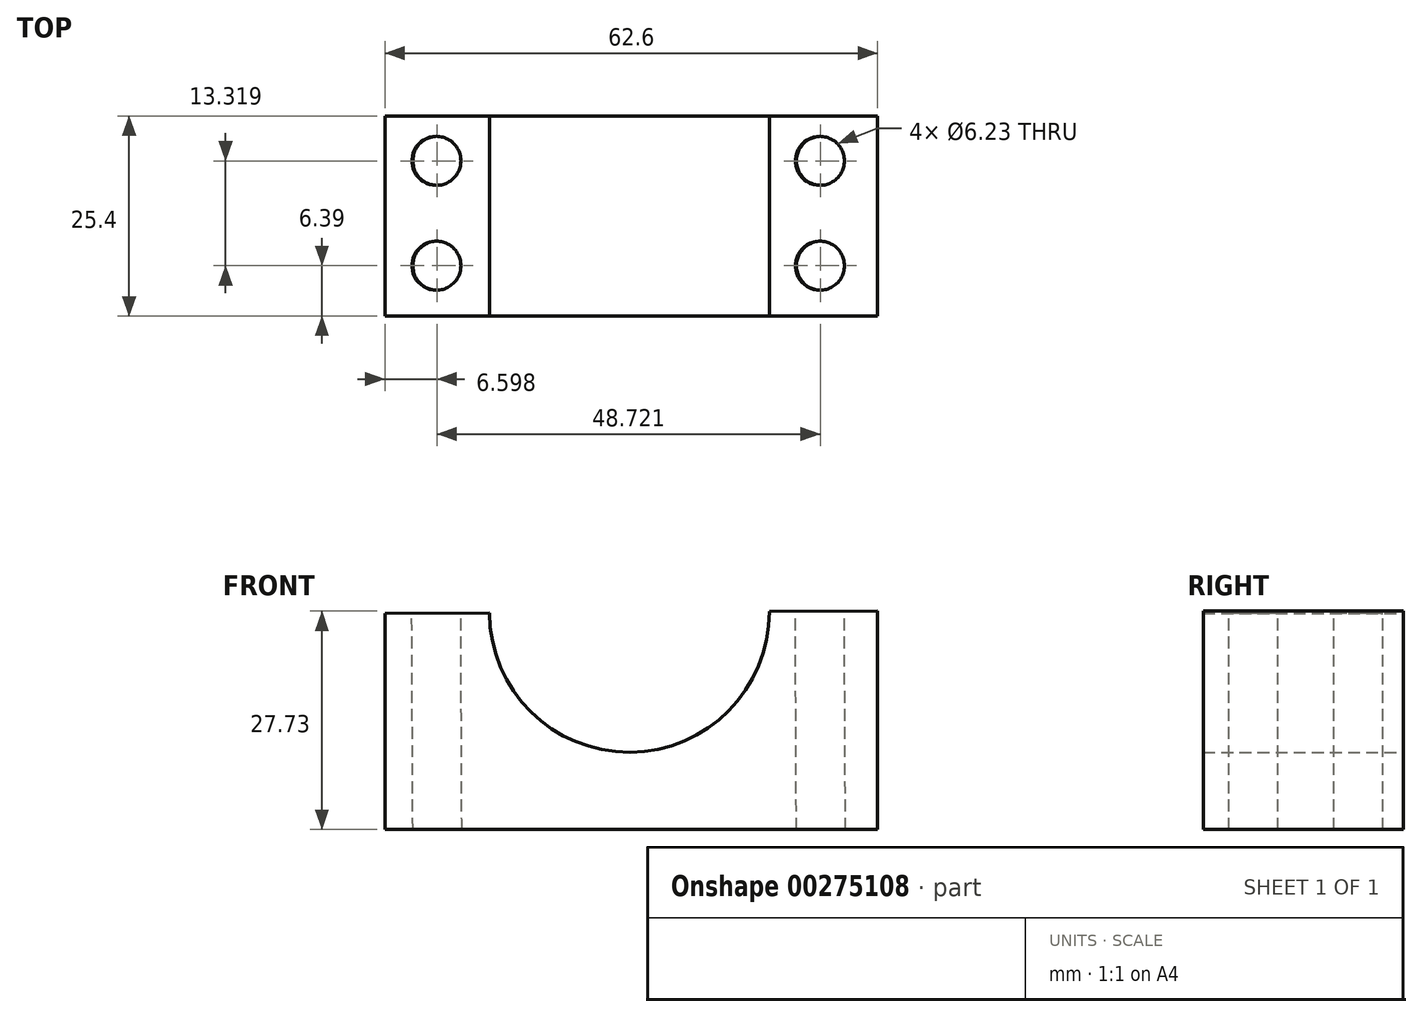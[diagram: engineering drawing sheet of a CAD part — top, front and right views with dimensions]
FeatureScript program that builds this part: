
annotation { "Feature Type Name" : "Feature", "Feature Type Description" : "" }
export const myFeature = defineFeature(function(context is Context, id is Id, definition is map)
    precondition{}
    {
        {
            var Q0;
            Q0=qCreatedBy(makeId("Front.planeOp"),FACE);
            var sketch = newSketch(context, id + "F0", { "sketchPlane" : qUnion([Q0])});
            skLineSegment(sketch, "E0.bottom", {"start": v(-31.05, 34.73) * mm, "end": v(-17.77, 34.79) * mm});
            skLineSegment(sketch, "E0.top", {"start": v(-31.05, 7.3) * mm, "end": v(31.55, 7.3) * mm});
            skLineSegment(sketch, "E0.left", {"start": v(-31.05, 34.73) * mm, "end": v(-31.05, 7.3) * mm});
            skLineSegment(sketch, "E0.right", {"start": v(31.55, 35.02) * mm, "end": v(31.55, 7.3) * mm});
            skArc(sketch, "E1", {"start": v(-17.77, 34.79) * mm, "mid": v(0.08, 17.1) * mm, "end": v(17.77, 34.96) * mm});
            skLineSegment(sketch, "E2.trimOffspring", {"start": v(17.77, 34.96) * mm, "end": v(31.55, 35.02) * mm});
            skSolve(sketch);
        }
        {
            var Q0;
            Q0 = qSketchRegion(id + "F0", true);
            extrude(context, id + "F1", {"entities" : qUnion([Q0]), "depth" : 25.4 * mm});
        }
        {
            var Q0;
            Q0=makeQuery(id+"F1.opExtrude","SWEPT_FACE",FACE,{"disambiguationData":[OSD([sQuery(id+"F0.wireOp",EDGE,"E2.trimOffspring")])]});
            var sketch = newSketch(context, id + "F2", { "sketchPlane" : qUnion([Q0])});
            skCircle(sketch, "E3", {"center": v(-24.35, -5.7) * mm, "radius": 3.11 * mm});
            skCircle(sketch, "E4", {"center": v(-24.35, -19.01) * mm, "radius": 3.11 * mm});
            skCircle(sketch, "E5", {"center": v(24.37, -5.7) * mm, "radius": 3.11 * mm});
            skCircle(sketch, "E6", {"center": v(24.37, -19.01) * mm, "radius": 3.11 * mm});
            skSolve(sketch);
        }
        {
            var Q0;
            Q0 = qSketchRegion(id + "F2", true);
            extrude(context, id + "F3", {"entities" : qUnion([Q0]), "operationType" : NewBodyOperationType.REMOVE, "endBound" : BoundingType.UP_TO_NEXT, "oppositeDirection" : true, "depth" : 25.4 * mm});
        }
    });
